# Revit family: EVID-4.2LP
name_source: partatom
category: Communication Devices
revit_build: Autodesk Revit 2017 (Build: 20160225_1515(x64)
units: mm (PartAtom-declared; Revit-internal decimal feet)

## family parameters
Always vertical = Yes
Cut with Voids When Loaded = No
Maintain Annotation Orientation = Yes
OmniClass Number = 23.85.10.11.11.21
OmniClass Title = Speakers
Part Type = Normal
Room Calculation Point = No
Round Connector Dimension = Use Diameter
Shared = No
Work Plane-Based = Yes

## types (1)
- EVIDC4.2LP_4"_Speaker_White
    ArchitectsAndEngineersSpecs = http://mtpvmc0059.us.bosch.com
    CTN = EVIDC4.2LP
    Default Elevation = 0 mm  [stored 0 ft]
    Depth = 94 mm  [stored 0.308399 ft]
    Description = Full bandwidth overload protection. Front baffle wattage tap adjustment. Includes tile bridge and mounting ring for easy installation. UL1480A and CSA 22.2 205 certified.
    Disclaimer = http://resource.boschsecurity.com
    FrontLength = 300 mm
    IfcExportAs = IfcBuildingElementProxy
    IfcExportType = IfcBuildingElementProxyType
    InstallationManual = http://mtpvmc0059.us.bosch.com
    Manufacturer = Electro Voice
    ManufacturerURL = https://www.electrovoice.com
    MaterialRALColour = RAL9010
    ModelNumber = F.01U.351.201
    PlanningTools = https://www.electrovoice.com
    ProductInformation = http://mtpvmc0059.us.bosch.com
    Uniclass2015Code = Pr_60_75_08_02

note: [stored X ft] marks values corroborated as IEEE doubles in the binary element streams (Revit-internal decimal feet)

## geometry (parser evidence)
native form markers: Blend x2, Sweep x3
no freeform markers — native parametric forms only
